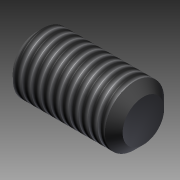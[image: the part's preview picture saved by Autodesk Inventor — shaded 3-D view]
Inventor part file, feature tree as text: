
AUTODESK INVENTOR PART (.ipt)
format: ipt  version: 2011 SP1 (Build 150282100, 282)  size: 117,248 bytes
history: native  units: mm
features: other x7, sketch x3, revolve x2, thread x1, extrude x1
ambient origin geometry x8: Origin, YZ Plane, XZ Plane, XY Plane, X Axis, Y Axis, Z Axis, Center Point
bodies: Solid1 (feature_tree)
feature tree (14):
  revolve  "Revolution1"  [1 undecoded]
  thread  "Thread1"  [1 undecoded]
  extrude  "Extrusion1"  TaperAngle=0.0deg  [1 undecoded]
  revolve  "Revolution2"  [1 undecoded]
  other  "CP_XY"
  other  "CP_YZ"
  other  "CP_ZX"
  other  "CP_X"
  other  "CP_Y"
  other  "CP_Z"
  other  "CP_Center"
  sketch  "Sketch_1"  dims[d0=360.0deg d1=7.7595mm d2=0.0mm d3=2.0mm d4=0.0mm]
  sketch  "Sketch_2"  dims[d5=360.0deg d6=0.0mm]
  sketch  "Sketch_3"
note: 4 required parameter values undecoded (feature->parameter linkage not recoverable at this tier; creation-order binding heuristic only, values carry confidence <= 0.55)